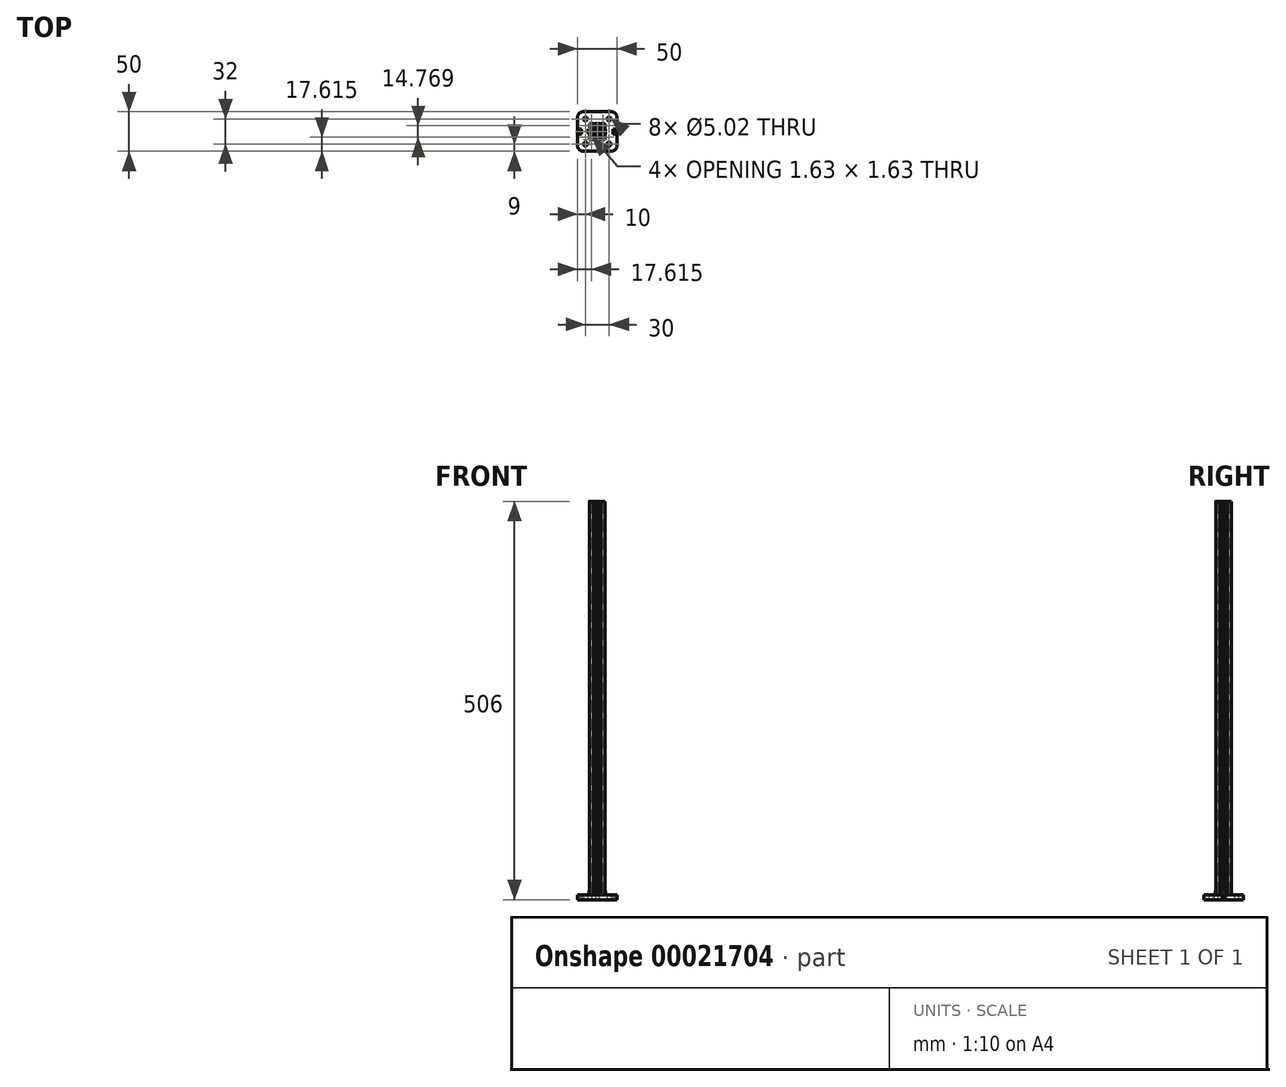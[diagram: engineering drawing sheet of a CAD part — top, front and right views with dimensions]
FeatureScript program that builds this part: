
annotation { "Feature Type Name" : "Feature", "Feature Type Description" : "" }
export const myFeature = defineFeature(function(context is Context, id is Id, definition is map)
    precondition{}
    {
        {
            var Q0;
            Q0=qCreatedBy(makeId("Top.planeOp"),FACE);
            var sketch = newSketch(context, id + "F4", { "sketchPlane" : qUnion([Q0])});
            skLineSegment(sketch, "E0", {"start": v(0, 0) * mm, "end": v(0, 25) * mm, "construction": true});
            skLineSegment(sketch, "E1", {"start": v(0, 0) * mm, "end": v(25, 0) * mm, "construction": true});
            skLineSegment(sketch, "E2", {"start": v(25, 0) * mm, "end": v(25, 18.3) * mm});
            skLineSegment(sketch, "E3", {"start": v(18.3, 25) * mm, "end": v(0, 25) * mm});
            skCircle(sketch, "E4", {"center": v(0, 0) * mm, "radius": 2.5 * mm, "construction": true});
            skLineSegment(sketch, "E5", {"start": v(15, 0) * mm, "end": v(15, 16) * mm, "construction": true});
            skLineSegment(sketch, "E6", {"start": v(15, 16) * mm, "end": v(0, 16) * mm, "construction": true});
            skCircle(sketch, "E7", {"center": v(15, 16) * mm, "radius": 2.5 * mm});
            skPoint(sketch, "E8.visualSharp", {"position": v(25, 25) * mm});
            skArc(sketch, "E8.filletArc", {"start": v(25, 18.3) * mm, "mid": v(23.04, 23.04) * mm, "end": v(18.3, 25) * mm});
            skLineSegment(sketch, "E9", {"start": v(22.26, 0) * mm, "end": v(22.26, 3.35) * mm});
            skLineSegment(sketch, "E10", {"start": v(22.26, 3.35) * mm, "end": v(25, 3.35) * mm});
            skLineSegment(sketch, "E11", {"start": v(22.26, 3.35) * mm, "end": v(20.26, 3.35) * mm});
            skLineSegment(sketch, "E12", {"start": v(20.26, 3.35) * mm, "end": v(20.26, 0) * mm});
            skCircle(sketch, "E13", {"center": v(10, 0) * mm, "radius": 2.5 * mm, "construction": true});
            skCircle(sketch, "E14", {"center": v(0, 10) * mm, "radius": 2.5 * mm, "construction": true});
            skLineSegment(sketch, "E15", {"start": v(10, 0) * mm, "end": v(0, 0) * mm, "construction": true});
            skLineSegment(sketch, "E16", {"start": v(0, 10) * mm, "end": v(0, 0) * mm, "construction": true});
            skArc(sketch, "E17", {"start": v(2.5, 0) * mm, "mid": v(1.77, 1.77) * mm, "end": v(0, 2.5) * mm});
            skArc(sketch, "E18", {"start": v(12.5, 0) * mm, "mid": v(10, 2.51) * mm, "end": v(7.5, 0) * mm});
            skArc(sketch, "E19", {"start": v(0, 7.5) * mm, "mid": v(2.5, 10) * mm, "end": v(0, 12.5) * mm});
            skArc(sketch, "E20.MirrorCS", {"start": v(0, 7.5) * mm, "mid": v(-2.5, 10) * mm, "end": v(0, 12.5) * mm});
            skArc(sketch, "E21.MirrorCS", {"start": v(-2.5, 0) * mm, "mid": v(-1.77, 1.77) * mm, "end": v(0, 2.5) * mm});
            skArc(sketch, "E22.MirrorCS", {"start": v(-12.5, 0) * mm, "mid": v(-10, 2.51) * mm, "end": v(-7.5, 0) * mm});
            skLineSegment(sketch, "E23.MirrorCS", {"start": v(-18.3, 25) * mm, "end": v(0, 25) * mm});
            skArc(sketch, "E24.MirrorCS", {"start": v(-25, 18.3) * mm, "mid": v(-23.04, 23.04) * mm, "end": v(-18.3, 25) * mm});
            skLineSegment(sketch, "E25.MirrorCS", {"start": v(-25, 0) * mm, "end": v(-25, 18.3) * mm});
            skLineSegment(sketch, "E26.MirrorCS", {"start": v(-22.26, 3.35) * mm, "end": v(-25, 3.35) * mm});
            skLineSegment(sketch, "E27.MirrorCS", {"start": v(-22.26, 0) * mm, "end": v(-22.26, 3.35) * mm});
            skLineSegment(sketch, "E28.MirrorCS", {"start": v(-22.26, 3.35) * mm, "end": v(-20.26, 3.35) * mm});
            skLineSegment(sketch, "E29.MirrorCS", {"start": v(-20.26, 3.35) * mm, "end": v(-20.26, 0) * mm});
            skCircle(sketch, "E30.MirrorC", {"center": v(-15, 16) * mm, "radius": 2.5 * mm});
            skLineSegment(sketch, "E31.MirrorCS", {"start": v(-25, 0) * mm, "end": v(-25, -18.3) * mm});
            skLineSegment(sketch, "E32.MirrorCS", {"start": v(-22.26, -3.35) * mm, "end": v(-25, -3.35) * mm});
            skLineSegment(sketch, "E33.MirrorCS", {"start": v(-22.26, 0) * mm, "end": v(-22.26, -3.35) * mm});
            skLineSegment(sketch, "E34.MirrorCS", {"start": v(-20.26, -3.35) * mm, "end": v(-20.26, 0) * mm});
            skLineSegment(sketch, "E35.MirrorCS", {"start": v(-22.26, -3.35) * mm, "end": v(-20.26, -3.35) * mm});
            skArc(sketch, "E36.MirrorCS", {"start": v(-12.5, 0) * mm, "mid": v(-10, -2.51) * mm, "end": v(-7.5, 0) * mm});
            skCircle(sketch, "E37.MirrorC", {"center": v(-15, -16) * mm, "radius": 2.5 * mm});
            skLineSegment(sketch, "E38.MirrorCS", {"start": v(-18.3, -25) * mm, "end": v(0, -25) * mm});
            skArc(sketch, "E39.MirrorCS", {"start": v(-25, -18.3) * mm, "mid": v(-23.04, -23.04) * mm, "end": v(-18.3, -25) * mm});
            skArc(sketch, "E40.MirrorCS", {"start": v(-2.5, 0) * mm, "mid": v(-1.77, -1.77) * mm, "end": v(0, -2.5) * mm});
            skArc(sketch, "E41.MirrorCS", {"start": v(2.5, 0) * mm, "mid": v(1.77, -1.77) * mm, "end": v(0, -2.5) * mm});
            skArc(sketch, "E42.MirrorCS", {"start": v(0, -7.5) * mm, "mid": v(2.5, -10) * mm, "end": v(0, -12.5) * mm});
            skArc(sketch, "E43.MirrorCS", {"start": v(0, -7.5) * mm, "mid": v(-2.5, -10) * mm, "end": v(0, -12.5) * mm});
            skArc(sketch, "E44.MirrorCS", {"start": v(12.5, 0) * mm, "mid": v(10, -2.51) * mm, "end": v(7.5, 0) * mm});
            skCircle(sketch, "E45.MirrorC", {"center": v(15, -16) * mm, "radius": 2.5 * mm});
            skLineSegment(sketch, "E46.MirrorCS", {"start": v(18.3, -25) * mm, "end": v(0, -25) * mm});
            skArc(sketch, "E47.MirrorCS", {"start": v(25, -18.3) * mm, "mid": v(23.04, -23.04) * mm, "end": v(18.3, -25) * mm});
            skLineSegment(sketch, "E48.MirrorCS", {"start": v(25, 0) * mm, "end": v(25, -18.3) * mm});
            skLineSegment(sketch, "E49.MirrorCS", {"start": v(20.26, -3.35) * mm, "end": v(20.26, 0) * mm});
            skLineSegment(sketch, "E50.MirrorCS", {"start": v(22.26, -3.35) * mm, "end": v(20.26, -3.35) * mm});
            skLineSegment(sketch, "E51.MirrorCS", {"start": v(22.26, 0) * mm, "end": v(22.26, -3.35) * mm});
            skLineSegment(sketch, "E52.MirrorCS", {"start": v(22.26, -3.35) * mm, "end": v(25, -3.35) * mm});
            skSolve(sketch);
        }
        {
            var Q0;
            Q0=makeQuery(id+"F4.imprint","IMPRINT",FACE,{"disambiguationData":[TD([[makeQuery(id+"F4.imprint","IMPRINT",EDGE,{"derivedFrom":sQuery(id+"F4.wireOp",EDGE,"E3")}),1.0]])]});
            var Q1;
            Q1=makeQuery(id+"F4.imprint","IMPRINT",FACE,{"disambiguationData":[TD([[makeQuery(id+"F4.imprint","IMPRINT",EDGE,{"derivedFrom":sQuery(id+"F4.wireOp",EDGE,"E22.MirrorCS")}),-1.0]])]});
            var Q2;
            Q2=makeQuery(id+"F4.imprint","IMPRINT",FACE,{"disambiguationData":[TD([[makeQuery(id+"F4.imprint","IMPRINT",EDGE,{"derivedFrom":sQuery(id+"F4.wireOp",EDGE,"E19")}),1.0]])]});
            var Q3;
            Q3=makeQuery(id+"F4.imprint","IMPRINT",FACE,{"disambiguationData":[TD([[makeQuery(id+"F4.imprint","IMPRINT",EDGE,{"derivedFrom":sQuery(id+"F4.wireOp",EDGE,"E18")}),1.0]])]});
            var Q4;
            Q4=makeQuery(id+"F4.imprint","IMPRINT",FACE,{"disambiguationData":[TD([[makeQuery(id+"F4.imprint","IMPRINT",EDGE,{"derivedFrom":sQuery(id+"F4.wireOp",EDGE,"E42.MirrorCS")}),-1.0]])]});
            extrude(context, id + "F0", {"entities" : qUnion([Q0, Q1, Q2, Q3, Q4]), "depth" : 6 * mm});
        }
        {
            var Q0;
            {var subQ4=sQuery(id+"F4.wireOp",EDGE,"E26.MirrorCS");Q0=makeQuery(id+"F4.imprint","IMPRINT",FACE,{"disambiguationData":[TD([[makeQuery(id+"F4.imprint","IMPRINT",EDGE,{"derivedFrom":subQ4}),1.0]])]});}
            var Q1;
            Q1=makeQuery(id+"F4.imprint","IMPRINT",FACE,{"disambiguationData":[TD([[makeQuery(id+"F4.imprint","IMPRINT",EDGE,{"derivedFrom":sQuery(id+"F4.wireOp",EDGE,"E9")}),-1.0]])]});
            extrude(context, id + "F5", {"entities" : qUnion([Q0, Q1]), "operationType" : NewBodyOperationType.ADD, "depth" : 4 * mm});
        }
        {
            var Q0;
            Q0=makeQuery(id+"F0.opExtrude","CAP_FACE",FACE,{"disambiguationData":[OSD([sQuery(id+"F4.wireOp",EDGE,"E2"),sQuery(id+"F4.wireOp",EDGE,"E3"),sQuery(id+"F4.wireOp",EDGE,"E7"),sQuery(id+"F4.wireOp",EDGE,"E8.filletArc"),sQuery(id+"F4.wireOp",EDGE,"E10"),sQuery(id+"F4.wireOp",EDGE,"E11"),sQuery(id+"F4.wireOp",EDGE,"E12"),sQuery(id+"F4.wireOp",EDGE,"E17"),sQuery(id+"F4.wireOp",EDGE,"E18"),sQuery(id+"F4.wireOp",EDGE,"E19"),sQuery(id+"F4.wireOp",EDGE,"E20.MirrorCS"),sQuery(id+"F4.wireOp",EDGE,"E21.MirrorCS"),sQuery(id+"F4.wireOp",EDGE,"E22.MirrorCS"),sQuery(id+"F4.wireOp",EDGE,"E23.MirrorCS"),sQuery(id+"F4.wireOp",EDGE,"E24.MirrorCS"),sQuery(id+"F4.wireOp",EDGE,"E25.MirrorCS"),sQuery(id+"F4.wireOp",EDGE,"E26.MirrorCS"),sQuery(id+"F4.wireOp",EDGE,"E28.MirrorCS"),sQuery(id+"F4.wireOp",EDGE,"E29.MirrorCS"),sQuery(id+"F4.wireOp",EDGE,"E30.MirrorC"),sQuery(id+"F4.wireOp",EDGE,"E31.MirrorCS"),sQuery(id+"F4.wireOp",EDGE,"E32.MirrorCS"),sQuery(id+"F4.wireOp",EDGE,"E34.MirrorCS"),sQuery(id+"F4.wireOp",EDGE,"E35.MirrorCS"),sQuery(id+"F4.wireOp",EDGE,"E36.MirrorCS"),sQuery(id+"F4.wireOp",EDGE,"E37.MirrorC"),sQuery(id+"F4.wireOp",EDGE,"E38.MirrorCS"),sQuery(id+"F4.wireOp",EDGE,"E39.MirrorCS"),sQuery(id+"F4.wireOp",EDGE,"E40.MirrorCS"),sQuery(id+"F4.wireOp",EDGE,"E41.MirrorCS"),sQuery(id+"F4.wireOp",EDGE,"E42.MirrorCS"),sQuery(id+"F4.wireOp",EDGE,"E43.MirrorCS"),sQuery(id+"F4.wireOp",EDGE,"E44.MirrorCS"),sQuery(id+"F4.wireOp",EDGE,"E45.MirrorC"),sQuery(id+"F4.wireOp",EDGE,"E46.MirrorCS"),sQuery(id+"F4.wireOp",EDGE,"E47.MirrorCS"),sQuery(id+"F4.wireOp",EDGE,"E48.MirrorCS"),sQuery(id+"F4.wireOp",EDGE,"E49.MirrorCS"),sQuery(id+"F4.wireOp",EDGE,"E50.MirrorCS"),sQuery(id+"F4.wireOp",EDGE,"E52.MirrorCS")])],"isStart":false});
            var sketch = newSketch(context, id + "F1", { "sketchPlane" : qUnion([Q0])});
            skLineSegment(sketch, "E53", {"start": v(2.73, 0) * mm, "end": v(-2.73, 0) * mm, "construction": true});
            skLineSegment(sketch, "E54", {"start": v(0, 2.73) * mm, "end": v(0, -2.73) * mm, "construction": true});
            skArc(sketch, "E55", {"start": v(-8.5, 10) * mm, "mid": v(-9.56, 9.56) * mm, "end": v(-10, 8.5) * mm});
            skLineSegment(sketch, "E56", {"start": v(-10, 8.5) * mm, "end": v(-10, 4.64) * mm});
            skLineSegment(sketch, "E57", {"start": v(-10, 4.64) * mm, "end": v(-8.2, 2.84) * mm});
            skLineSegment(sketch, "E58", {"start": v(-8.2, 5.5) * mm, "end": v(-8.2, 2.84) * mm});
            skLineSegment(sketch, "E59", {"start": v(-8.2, 5.5) * mm, "end": v(-6.56, 5.5) * mm});
            skLineSegment(sketch, "E60", {"start": v(-6.56, 5.5) * mm, "end": v(-3.9, 2.84) * mm});
            skLineSegment(sketch, "E61", {"start": v(-3.9, 2.84) * mm, "end": v(-3.9, 0.2) * mm});
            skLineSegment(sketch, "E62", {"start": v(-3.9, 0.2) * mm, "end": v(-3.7, 0) * mm});
            skLineSegment(sketch, "E63", {"start": v(-0.2, 3.9) * mm, "end": v(0, 3.7) * mm});
            skLineSegment(sketch, "E64", {"start": v(-0.2, 3.9) * mm, "end": v(-2.84, 3.9) * mm});
            skLineSegment(sketch, "E65", {"start": v(-5.5, 6.56) * mm, "end": v(-2.84, 3.9) * mm});
            skLineSegment(sketch, "E66", {"start": v(-5.5, 8.2) * mm, "end": v(-5.5, 6.56) * mm});
            skLineSegment(sketch, "E67", {"start": v(-2.84, 8.2) * mm, "end": v(-5.5, 8.2) * mm});
            skLineSegment(sketch, "E68", {"start": v(-4.64, 10) * mm, "end": v(-2.84, 8.2) * mm});
            skLineSegment(sketch, "E69", {"start": v(-8.5, 10) * mm, "end": v(-4.64, 10) * mm});
            skCircle(sketch, "E70", {"center": v(0, 0) * mm, "radius": 2.1 * mm});
            skLineSegment(sketch, "E71", {"start": v(-6.57, 8.2) * mm, "end": v(-8.2, 8.2) * mm});
            skLineSegment(sketch, "E72", {"start": v(-6.57, 8.2) * mm, "end": v(-6.57, 7.63) * mm});
            skLineSegment(sketch, "E73", {"start": v(-7.63, 6.57) * mm, "end": v(-6.57, 7.63) * mm});
            skLineSegment(sketch, "E74", {"start": v(-8.2, 6.57) * mm, "end": v(-7.63, 6.57) * mm});
            skLineSegment(sketch, "E75", {"start": v(-8.2, 8.2) * mm, "end": v(-8.2, 6.57) * mm});
            skLineSegment(sketch, "E76.MirrorCS", {"start": v(0.2, 3.9) * mm, "end": v(0, 3.7) * mm});
            skLineSegment(sketch, "E77.MirrorCS", {"start": v(0.2, 3.9) * mm, "end": v(2.84, 3.9) * mm});
            skLineSegment(sketch, "E78.MirrorCS", {"start": v(5.5, 6.56) * mm, "end": v(2.84, 3.9) * mm});
            skLineSegment(sketch, "E79.MirrorCS", {"start": v(5.5, 8.2) * mm, "end": v(5.5, 6.56) * mm});
            skLineSegment(sketch, "E80.MirrorCS", {"start": v(2.84, 8.2) * mm, "end": v(5.5, 8.2) * mm});
            skLineSegment(sketch, "E81.MirrorCS", {"start": v(4.64, 10) * mm, "end": v(2.84, 8.2) * mm});
            skLineSegment(sketch, "E82.MirrorCS", {"start": v(8.5, 10) * mm, "end": v(4.64, 10) * mm});
            skArc(sketch, "E83.MirrorCS", {"start": v(8.5, 10) * mm, "mid": v(9.56, 9.56) * mm, "end": v(10, 8.5) * mm});
            skLineSegment(sketch, "E84.MirrorCS", {"start": v(10, 8.5) * mm, "end": v(10, 4.64) * mm});
            skLineSegment(sketch, "E85.MirrorCS", {"start": v(8.2, 8.2) * mm, "end": v(8.2, 6.57) * mm});
            skLineSegment(sketch, "E86.MirrorCS", {"start": v(6.57, 8.2) * mm, "end": v(8.2, 8.2) * mm});
            skLineSegment(sketch, "E87.MirrorCS", {"start": v(6.57, 8.2) * mm, "end": v(6.57, 7.63) * mm});
            skLineSegment(sketch, "E88.MirrorCS", {"start": v(7.63, 6.57) * mm, "end": v(6.57, 7.63) * mm});
            skLineSegment(sketch, "E89.MirrorCS", {"start": v(8.2, 6.57) * mm, "end": v(7.63, 6.57) * mm});
            skLineSegment(sketch, "E90.MirrorCS", {"start": v(10, 4.64) * mm, "end": v(8.2, 2.84) * mm});
            skLineSegment(sketch, "E91.MirrorCS", {"start": v(8.2, 5.5) * mm, "end": v(8.2, 2.84) * mm});
            skLineSegment(sketch, "E92.MirrorCS", {"start": v(8.2, 5.5) * mm, "end": v(6.56, 5.5) * mm});
            skLineSegment(sketch, "E93.MirrorCS", {"start": v(6.56, 5.5) * mm, "end": v(3.9, 2.84) * mm});
            skLineSegment(sketch, "E94.MirrorCS", {"start": v(3.9, 2.84) * mm, "end": v(3.9, 0.2) * mm});
            skLineSegment(sketch, "E95.MirrorCS", {"start": v(3.9, 0.2) * mm, "end": v(3.7, 0) * mm});
            skLineSegment(sketch, "E96.MirrorCS", {"start": v(3.9, -0.2) * mm, "end": v(3.7, 0) * mm});
            skLineSegment(sketch, "E97.MirrorCS", {"start": v(6.57, -8.2) * mm, "end": v(6.57, -7.63) * mm});
            skLineSegment(sketch, "E98.MirrorCS", {"start": v(8.2, -6.57) * mm, "end": v(7.63, -6.57) * mm});
            skLineSegment(sketch, "E99.MirrorCS", {"start": v(7.63, -6.57) * mm, "end": v(6.57, -7.63) * mm});
            skLineSegment(sketch, "E100.MirrorCS", {"start": v(5.5, -8.2) * mm, "end": v(5.5, -6.56) * mm});
            skLineSegment(sketch, "E101.MirrorCS", {"start": v(4.64, -10) * mm, "end": v(2.84, -8.2) * mm});
            skLineSegment(sketch, "E102.MirrorCS", {"start": v(2.84, -8.2) * mm, "end": v(5.5, -8.2) * mm});
            skLineSegment(sketch, "E103.MirrorCS", {"start": v(10, -8.5) * mm, "end": v(10, -4.64) * mm});
            skLineSegment(sketch, "E104.MirrorCS", {"start": v(8.2, -5.5) * mm, "end": v(6.56, -5.5) * mm});
            skLineSegment(sketch, "E105.MirrorCS", {"start": v(5.5, -6.56) * mm, "end": v(2.84, -3.9) * mm});
            skLineSegment(sketch, "E106.MirrorCS", {"start": v(8.2, -8.2) * mm, "end": v(8.2, -6.57) * mm});
            skLineSegment(sketch, "E107.MirrorCS", {"start": v(8.2, -5.5) * mm, "end": v(8.2, -2.84) * mm});
            skLineSegment(sketch, "E108.MirrorCS", {"start": v(6.56, -5.5) * mm, "end": v(3.9, -2.84) * mm});
            skArc(sketch, "E109.MirrorCS", {"start": v(8.5, -10) * mm, "mid": v(9.56, -9.56) * mm, "end": v(10, -8.5) * mm});
            skLineSegment(sketch, "E110.MirrorCS", {"start": v(10, -4.64) * mm, "end": v(8.2, -2.84) * mm});
            skLineSegment(sketch, "E111.MirrorCS", {"start": v(6.57, -8.2) * mm, "end": v(8.2, -8.2) * mm});
            skLineSegment(sketch, "E112.MirrorCS", {"start": v(8.5, -10) * mm, "end": v(4.64, -10) * mm});
            skLineSegment(sketch, "E113.MirrorCS", {"start": v(3.9, -2.84) * mm, "end": v(3.9, -0.2) * mm});
            skLineSegment(sketch, "E114.MirrorCS", {"start": v(0.2, -3.9) * mm, "end": v(2.84, -3.9) * mm});
            skLineSegment(sketch, "E115.MirrorCS", {"start": v(0.2, -3.9) * mm, "end": v(0, -3.7) * mm});
            skLineSegment(sketch, "E116.MirrorCS", {"start": v(-0.2, -3.9) * mm, "end": v(0, -3.7) * mm});
            skLineSegment(sketch, "E117.MirrorCS", {"start": v(-0.2, -3.9) * mm, "end": v(-2.84, -3.9) * mm});
            skLineSegment(sketch, "E118.MirrorCS", {"start": v(-5.5, -6.56) * mm, "end": v(-2.84, -3.9) * mm});
            skLineSegment(sketch, "E119.MirrorCS", {"start": v(-5.5, -8.2) * mm, "end": v(-5.5, -6.56) * mm});
            skLineSegment(sketch, "E120.MirrorCS", {"start": v(-4.64, -10) * mm, "end": v(-2.84, -8.2) * mm});
            skLineSegment(sketch, "E121.MirrorCS", {"start": v(-2.84, -8.2) * mm, "end": v(-5.5, -8.2) * mm});
            skLineSegment(sketch, "E122.MirrorCS", {"start": v(-8.5, -10) * mm, "end": v(-4.64, -10) * mm});
            skArc(sketch, "E123.MirrorCS", {"start": v(-8.5, -10) * mm, "mid": v(-9.56, -9.56) * mm, "end": v(-10, -8.5) * mm});
            skLineSegment(sketch, "E124.MirrorCS", {"start": v(-10, -8.5) * mm, "end": v(-10, -4.64) * mm});
            skLineSegment(sketch, "E125.MirrorCS", {"start": v(-8.2, -5.5) * mm, "end": v(-8.2, -2.84) * mm});
            skLineSegment(sketch, "E126.MirrorCS", {"start": v(-10, -4.64) * mm, "end": v(-8.2, -2.84) * mm});
            skLineSegment(sketch, "E127.MirrorCS", {"start": v(-8.2, -8.2) * mm, "end": v(-8.2, -6.57) * mm});
            skLineSegment(sketch, "E128.MirrorCS", {"start": v(-6.57, -8.2) * mm, "end": v(-8.2, -8.2) * mm});
            skLineSegment(sketch, "E129.MirrorCS", {"start": v(-6.57, -8.2) * mm, "end": v(-6.57, -7.63) * mm});
            skLineSegment(sketch, "E130.MirrorCS", {"start": v(-7.63, -6.57) * mm, "end": v(-6.57, -7.63) * mm});
            skLineSegment(sketch, "E131.MirrorCS", {"start": v(-8.2, -6.57) * mm, "end": v(-7.63, -6.57) * mm});
            skLineSegment(sketch, "E132.MirrorCS", {"start": v(-8.2, -5.5) * mm, "end": v(-6.56, -5.5) * mm});
            skLineSegment(sketch, "E133.MirrorCS", {"start": v(-6.56, -5.5) * mm, "end": v(-3.9, -2.84) * mm});
            skLineSegment(sketch, "E134.MirrorCS", {"start": v(-3.9, -2.84) * mm, "end": v(-3.9, -0.2) * mm});
            skLineSegment(sketch, "E135.MirrorCS", {"start": v(-3.9, -0.2) * mm, "end": v(-3.7, 0) * mm});
            skLineSegment(sketch, "E136.0", {"start": v(-5.1, 6.52) * mm, "end": v(-2.88, 4.3) * mm});
            skLineSegment(sketch, "E137.0", {"start": v(-5.25, 7.45) * mm, "end": v(-5.25, 6.87) * mm});
            skLineSegment(sketch, "E138.0", {"start": v(-2.84, 7.95) * mm, "end": v(-4.75, 7.95) * mm});
            skLineSegment(sketch, "E139.0", {"start": v(0, 4.15) * mm, "end": v(-2.53, 4.15) * mm});
            skLineSegment(sketch, "E140", {"start": v(0, 2.73) * mm, "end": v(0, 14.28) * mm, "construction": true});
            skLineSegment(sketch, "E141.MirrorCS", {"start": v(2.84, 7.95) * mm, "end": v(4.75, 7.95) * mm});
            skLineSegment(sketch, "E142.MirrorCS", {"start": v(5.25, 7.45) * mm, "end": v(5.25, 6.87) * mm});
            skLineSegment(sketch, "E143.MirrorCS", {"start": v(5.1, 6.52) * mm, "end": v(2.88, 4.3) * mm});
            skLineSegment(sketch, "E144.MirrorCS", {"start": v(0, 4.15) * mm, "end": v(2.53, 4.15) * mm});
            skLineSegment(sketch, "E145", {"start": v(0, 0) * mm, "end": v(8.5, 8.5) * mm, "construction": true});
            skLineSegment(sketch, "E146", {"start": v(8.5, -8.5) * mm, "end": v(-8.5, 8.5) * mm, "construction": true});
            skLineSegment(sketch, "E147.0", {"start": v(-3.6, 9.32) * mm, "end": v(-2.66, 8.38) * mm});
            skPoint(sketch, "E148.newPointB", {"position": v(0, 7.95) * mm});
            skArc(sketch, "E148.filletArc", {"start": v(-2.84, 7.95) * mm, "mid": v(-2.6, 8.1) * mm, "end": v(-2.66, 8.38) * mm});
            skLineSegment(sketch, "E149", {"start": v(-3.26, 10.18) * mm, "end": v(0, 10.18) * mm});
            skArc(sketch, "E150.MirrorCS", {"start": v(2.84, 7.95) * mm, "mid": v(2.6, 8.1) * mm, "end": v(2.66, 8.38) * mm});
            skLineSegment(sketch, "E151.MirrorCS", {"start": v(3.26, 10.18) * mm, "end": v(0, 10.18) * mm});
            skLineSegment(sketch, "E152.MirrorCS", {"start": v(3.6, 9.32) * mm, "end": v(2.66, 8.38) * mm});
            skPoint(sketch, "E153.visualSharp", {"position": v(-4.46, 10.18) * mm});
            skArc(sketch, "E153.filletArc", {"start": v(-3.26, 10.18) * mm, "mid": v(-3.72, 9.87) * mm, "end": v(-3.6, 9.32) * mm});
            skPoint(sketch, "E154.visualSharp", {"position": v(4.46, 10.18) * mm});
            skArc(sketch, "E154.filletArc", {"start": v(3.6, 9.32) * mm, "mid": v(3.72, 9.87) * mm, "end": v(3.26, 10.18) * mm});
            skPoint(sketch, "E155.visualSharp", {"position": v(5.25, 7.95) * mm});
            skArc(sketch, "E155.filletArc", {"start": v(5.25, 7.45) * mm, "mid": v(5.1, 7.8) * mm, "end": v(4.75, 7.95) * mm});
            skPoint(sketch, "E156.visualSharp", {"position": v(5.25, 6.66) * mm});
            skArc(sketch, "E156.filletArc", {"start": v(5.1, 6.52) * mm, "mid": v(5.21, 6.68) * mm, "end": v(5.25, 6.87) * mm});
            skPoint(sketch, "E157.visualSharp", {"position": v(2.74, 4.15) * mm});
            skArc(sketch, "E157.filletArc", {"start": v(2.53, 4.15) * mm, "mid": v(2.72, 4.19) * mm, "end": v(2.88, 4.3) * mm});
            skPoint(sketch, "E158.visualSharp", {"position": v(-2.74, 4.15) * mm});
            skArc(sketch, "E158.filletArc", {"start": v(-2.88, 4.3) * mm, "mid": v(-2.72, 4.19) * mm, "end": v(-2.53, 4.15) * mm});
            skPoint(sketch, "E159.visualSharp", {"position": v(-5.25, 6.66) * mm});
            skArc(sketch, "E159.filletArc", {"start": v(-5.25, 6.87) * mm, "mid": v(-5.21, 6.68) * mm, "end": v(-5.1, 6.52) * mm});
            skPoint(sketch, "E160.visualSharp", {"position": v(-5.25, 7.95) * mm});
            skArc(sketch, "E160.filletArc", {"start": v(-4.75, 7.95) * mm, "mid": v(-5.1, 7.8) * mm, "end": v(-5.25, 7.45) * mm});
            skLineSegment(sketch, "E161.1.0", {"start": v(-10.18, -3.26) * mm, "end": v(-10.18, 0) * mm});
            skArc(sketch, "E161.1.1", {"start": v(-10.18, -3.26) * mm, "mid": v(-9.87, -3.72) * mm, "end": v(-9.32, -3.6) * mm});
            skLineSegment(sketch, "E161.1.2", {"start": v(-9.32, -3.6) * mm, "end": v(-8.38, -2.66) * mm});
            skArc(sketch, "E161.1.3", {"start": v(-7.95, -2.84) * mm, "mid": v(-8.1, -2.6) * mm, "end": v(-8.38, -2.66) * mm});
            skLineSegment(sketch, "E161.1.4", {"start": v(-7.95, -2.84) * mm, "end": v(-7.95, -4.75) * mm});
            skArc(sketch, "E161.1.5", {"start": v(-7.95, -4.75) * mm, "mid": v(-7.8, -5.1) * mm, "end": v(-7.45, -5.25) * mm});
            skLineSegment(sketch, "E161.1.6", {"start": v(-7.45, -5.25) * mm, "end": v(-6.87, -5.25) * mm});
            skArc(sketch, "E161.1.7", {"start": v(-6.87, -5.25) * mm, "mid": v(-6.68, -5.21) * mm, "end": v(-6.52, -5.1) * mm});
            skLineSegment(sketch, "E161.1.8", {"start": v(-6.52, -5.1) * mm, "end": v(-4.3, -2.88) * mm});
            skArc(sketch, "E161.1.9", {"start": v(-4.3, -2.88) * mm, "mid": v(-4.19, -2.72) * mm, "end": v(-4.15, -2.53) * mm});
            skLineSegment(sketch, "E161.1.10", {"start": v(-4.15, 0) * mm, "end": v(-4.15, -2.53) * mm});
            skLineSegment(sketch, "E161.1.11", {"start": v(-4.15, 0) * mm, "end": v(-4.15, 2.53) * mm});
            skArc(sketch, "E161.1.12", {"start": v(-4.15, 2.53) * mm, "mid": v(-4.19, 2.72) * mm, "end": v(-4.3, 2.88) * mm});
            skLineSegment(sketch, "E161.1.13", {"start": v(-6.52, 5.1) * mm, "end": v(-4.3, 2.88) * mm});
            skArc(sketch, "E161.1.14", {"start": v(-6.52, 5.1) * mm, "mid": v(-6.68, 5.21) * mm, "end": v(-6.87, 5.25) * mm});
            skLineSegment(sketch, "E161.1.15", {"start": v(-7.45, 5.25) * mm, "end": v(-6.87, 5.25) * mm});
            skArc(sketch, "E161.1.16", {"start": v(-7.45, 5.25) * mm, "mid": v(-7.8, 5.1) * mm, "end": v(-7.95, 4.75) * mm});
            skLineSegment(sketch, "E161.1.17", {"start": v(-7.95, 2.84) * mm, "end": v(-7.95, 4.75) * mm});
            skArc(sketch, "E161.1.18", {"start": v(-7.95, 2.84) * mm, "mid": v(-8.1, 2.6) * mm, "end": v(-8.38, 2.66) * mm});
            skLineSegment(sketch, "E161.1.19", {"start": v(-9.32, 3.6) * mm, "end": v(-8.38, 2.66) * mm});
            skArc(sketch, "E161.1.20", {"start": v(-9.32, 3.6) * mm, "mid": v(-9.87, 3.72) * mm, "end": v(-10.18, 3.26) * mm});
            skLineSegment(sketch, "E161.1.21", {"start": v(-10.18, 3.26) * mm, "end": v(-10.18, 0) * mm});
            skLineSegment(sketch, "E161.2.0", {"start": v(3.26, -10.18) * mm, "end": v(0, -10.18) * mm});
            skArc(sketch, "E161.2.1", {"start": v(3.26, -10.18) * mm, "mid": v(3.72, -9.87) * mm, "end": v(3.6, -9.32) * mm});
            skLineSegment(sketch, "E161.2.2", {"start": v(3.6, -9.32) * mm, "end": v(2.66, -8.38) * mm});
            skArc(sketch, "E161.2.3", {"start": v(2.84, -7.95) * mm, "mid": v(2.6, -8.1) * mm, "end": v(2.66, -8.38) * mm});
            skLineSegment(sketch, "E161.2.4", {"start": v(2.84, -7.95) * mm, "end": v(4.75, -7.95) * mm});
            skArc(sketch, "E161.2.5", {"start": v(4.75, -7.95) * mm, "mid": v(5.1, -7.8) * mm, "end": v(5.25, -7.45) * mm});
            skLineSegment(sketch, "E161.2.6", {"start": v(5.25, -7.45) * mm, "end": v(5.25, -6.87) * mm});
            skArc(sketch, "E161.2.7", {"start": v(5.25, -6.87) * mm, "mid": v(5.21, -6.68) * mm, "end": v(5.1, -6.52) * mm});
            skLineSegment(sketch, "E161.2.8", {"start": v(5.1, -6.52) * mm, "end": v(2.88, -4.3) * mm});
            skArc(sketch, "E161.2.9", {"start": v(2.88, -4.3) * mm, "mid": v(2.72, -4.19) * mm, "end": v(2.53, -4.15) * mm});
            skLineSegment(sketch, "E161.2.10", {"start": v(0, -4.15) * mm, "end": v(2.53, -4.15) * mm});
            skLineSegment(sketch, "E161.2.11", {"start": v(0, -4.15) * mm, "end": v(-2.53, -4.15) * mm});
            skArc(sketch, "E161.2.12", {"start": v(-2.53, -4.15) * mm, "mid": v(-2.72, -4.19) * mm, "end": v(-2.88, -4.3) * mm});
            skLineSegment(sketch, "E161.2.13", {"start": v(-5.1, -6.52) * mm, "end": v(-2.88, -4.3) * mm});
            skArc(sketch, "E161.2.14", {"start": v(-5.1, -6.52) * mm, "mid": v(-5.21, -6.68) * mm, "end": v(-5.25, -6.87) * mm});
            skLineSegment(sketch, "E161.2.15", {"start": v(-5.25, -7.45) * mm, "end": v(-5.25, -6.87) * mm});
            skArc(sketch, "E161.2.16", {"start": v(-5.25, -7.45) * mm, "mid": v(-5.1, -7.8) * mm, "end": v(-4.75, -7.95) * mm});
            skLineSegment(sketch, "E161.2.17", {"start": v(-2.84, -7.95) * mm, "end": v(-4.75, -7.95) * mm});
            skArc(sketch, "E161.2.18", {"start": v(-2.84, -7.95) * mm, "mid": v(-2.6, -8.1) * mm, "end": v(-2.66, -8.38) * mm});
            skLineSegment(sketch, "E161.2.19", {"start": v(-3.6, -9.32) * mm, "end": v(-2.66, -8.38) * mm});
            skArc(sketch, "E161.2.20", {"start": v(-3.6, -9.32) * mm, "mid": v(-3.72, -9.87) * mm, "end": v(-3.26, -10.18) * mm});
            skLineSegment(sketch, "E161.2.21", {"start": v(-3.26, -10.18) * mm, "end": v(0, -10.18) * mm});
            skLineSegment(sketch, "E161.3.0", {"start": v(10.18, 3.26) * mm, "end": v(10.18, 0) * mm});
            skArc(sketch, "E161.3.1", {"start": v(10.18, 3.26) * mm, "mid": v(9.87, 3.72) * mm, "end": v(9.32, 3.6) * mm});
            skLineSegment(sketch, "E161.3.2", {"start": v(9.32, 3.6) * mm, "end": v(8.38, 2.66) * mm});
            skArc(sketch, "E161.3.3", {"start": v(7.95, 2.84) * mm, "mid": v(8.1, 2.6) * mm, "end": v(8.38, 2.66) * mm});
            skLineSegment(sketch, "E161.3.4", {"start": v(7.95, 2.84) * mm, "end": v(7.95, 4.75) * mm});
            skArc(sketch, "E161.3.5", {"start": v(7.95, 4.75) * mm, "mid": v(7.8, 5.1) * mm, "end": v(7.45, 5.25) * mm});
            skLineSegment(sketch, "E161.3.6", {"start": v(7.45, 5.25) * mm, "end": v(6.87, 5.25) * mm});
            skArc(sketch, "E161.3.7", {"start": v(6.87, 5.25) * mm, "mid": v(6.68, 5.21) * mm, "end": v(6.52, 5.1) * mm});
            skLineSegment(sketch, "E161.3.8", {"start": v(6.52, 5.1) * mm, "end": v(4.3, 2.88) * mm});
            skArc(sketch, "E161.3.9", {"start": v(4.3, 2.88) * mm, "mid": v(4.19, 2.72) * mm, "end": v(4.15, 2.53) * mm});
            skLineSegment(sketch, "E161.3.10", {"start": v(4.15, 0) * mm, "end": v(4.15, 2.53) * mm});
            skLineSegment(sketch, "E161.3.11", {"start": v(4.15, 0) * mm, "end": v(4.15, -2.53) * mm});
            skArc(sketch, "E161.3.12", {"start": v(4.15, -2.53) * mm, "mid": v(4.19, -2.72) * mm, "end": v(4.3, -2.88) * mm});
            skLineSegment(sketch, "E161.3.13", {"start": v(6.52, -5.1) * mm, "end": v(4.3, -2.88) * mm});
            skArc(sketch, "E161.3.14", {"start": v(6.52, -5.1) * mm, "mid": v(6.68, -5.21) * mm, "end": v(6.87, -5.25) * mm});
            skLineSegment(sketch, "E161.3.15", {"start": v(7.45, -5.25) * mm, "end": v(6.87, -5.25) * mm});
            skArc(sketch, "E161.3.16", {"start": v(7.45, -5.25) * mm, "mid": v(7.8, -5.1) * mm, "end": v(7.95, -4.75) * mm});
            skLineSegment(sketch, "E161.3.17", {"start": v(7.95, -2.84) * mm, "end": v(7.95, -4.75) * mm});
            skArc(sketch, "E161.3.18", {"start": v(7.95, -2.84) * mm, "mid": v(8.1, -2.6) * mm, "end": v(8.38, -2.66) * mm});
            skLineSegment(sketch, "E161.3.19", {"start": v(9.32, -3.6) * mm, "end": v(8.38, -2.66) * mm});
            skArc(sketch, "E161.3.20", {"start": v(9.32, -3.6) * mm, "mid": v(9.87, -3.72) * mm, "end": v(10.18, -3.26) * mm});
            skLineSegment(sketch, "E161.3.21", {"start": v(10.18, -3.26) * mm, "end": v(10.18, 0) * mm});
            skSolve(sketch);
        }
        {
            var Q0;
            Q0=makeQuery(id+"F1.imprint","IMPRINT",FACE,{"disambiguationData":[TD([[makeQuery(id+"F1.imprint","IMPRINT",EDGE,{"derivedFrom":sQuery(id+"F1.wireOp",EDGE,"E136.0")}),1.0]])]});
            var Q1;
            Q1=makeQuery(id+"F1.imprint","IMPRINT",FACE,{"disambiguationData":[TD([[makeQuery(id+"F1.imprint","IMPRINT",EDGE,{"derivedFrom":sQuery(id+"F1.wireOp",EDGE,"97a04347-ffc2-4272-8581-b63b87e191c30.MirrorCS")}),1.0]])]});
            var Q2;
            {var subQ6=sQuery(id+"F1.wireOp",EDGE,"b754c6b4-6ef1-42a1-b540-394828c441de0.MirrorCS");Q2=makeQuery(id+"F1.imprint","IMPRINT",FACE,{"disambiguationData":[TD([[makeQuery(id+"F1.imprint","IMPRINT",EDGE,{"derivedFrom":subQ6}),-1.0]])]});}
            var Q3;
            Q3=makeQuery(id+"F1.imprint","IMPRINT",FACE,{"disambiguationData":[TD([[makeQuery(id+"F1.imprint","IMPRINT",EDGE,{"derivedFrom":sQuery(id+"F1.wireOp",EDGE,"dc0c365e-7566-4fdd-9898-c21d8e3a59930.MirrorCS")}),1.0]])]});
            var Q4;
            {var subQ1=sQuery(id+"F1.wireOp",EDGE,"E141.MirrorCS");var subQ3=sQuery(id+"F1.wireOp",EDGE,"E138.0");var subQ5=makeQuery(id+"F1.imprint","INTERSECT",VERTEX,{"derivedFrom":[subQ3,subQ1]});Q4=makeQuery(id+"F1.imprint","IMPRINT",FACE,{"disambiguationData":[TD([[makeQuery(id+"F1.imprint","IMPRINT",EDGE,{"disambiguationData":[TD([[subQ5,-1.0]])],"derivedFrom":subQ3}),1.0]])]});}
            var Q5;
            {var subQ1=sQuery(id+"F1.wireOp",EDGE,"4a798bb9-35ed-405a-be8e-6beaa67aea9b0.MirrorCS");var subQ3=sQuery(id+"F1.wireOp",EDGE,"765a75a6-8426-4268-bcc0-7f65aa6ce5040.MirrorCS");var subQ5=makeQuery(id+"F1.imprint","INTERSECT",VERTEX,{"derivedFrom":[subQ3,subQ1]});Q5=makeQuery(id+"F1.imprint","IMPRINT",FACE,{"disambiguationData":[TD([[makeQuery(id+"F1.imprint","IMPRINT",EDGE,{"disambiguationData":[TD([[subQ5,-1.0]])],"derivedFrom":subQ3}),1.0]])]});}
            var Q6;
            {var subQ1=sQuery(id+"F1.wireOp",EDGE,"61109fae-0632-4fd6-96c0-1158d4c46b1f0.MirrorCS");var subQ3=sQuery(id+"F1.wireOp",EDGE,"6bdf6139-cb56-45af-9e7b-c82a8b494dab0.MirrorCS");var subQ5=makeQuery(id+"F1.imprint","INTERSECT",VERTEX,{"derivedFrom":[subQ3,subQ1]});Q6=makeQuery(id+"F1.imprint","IMPRINT",FACE,{"disambiguationData":[TD([[makeQuery(id+"F1.imprint","IMPRINT",EDGE,{"disambiguationData":[TD([[subQ5,-1.0]])],"derivedFrom":subQ3}),-1.0]])]});}
            var Q7;
            {var subQ1=sQuery(id+"F1.wireOp",EDGE,"5f06026f-91d5-4f2f-9c34-d27ebdce79bf0.MirrorCS");var subQ3=sQuery(id+"F1.wireOp",EDGE,"f246371d-f16e-4b79-9ad7-26af30ad1bcb0.MirrorCS");var subQ5=makeQuery(id+"F1.imprint","INTERSECT",VERTEX,{"derivedFrom":[subQ3,subQ1]});Q7=makeQuery(id+"F1.imprint","IMPRINT",FACE,{"disambiguationData":[TD([[makeQuery(id+"F1.imprint","IMPRINT",EDGE,{"disambiguationData":[TD([[subQ5,-1.0]])],"derivedFrom":subQ3}),-1.0]])]});}
            var Q8;
            Q8=makeQuery(id+"F1.imprint","IMPRINT",FACE,{"disambiguationData":[TD([[makeQuery(id+"F1.imprint","IMPRINT",EDGE,{"derivedFrom":sQuery(id+"F1.wireOp",EDGE,"E161.1.0")}),-1.0]])]});
            var Q9;
            Q9=makeQuery(id+"F1.imprint","IMPRINT",FACE,{"disambiguationData":[TD([[makeQuery(id+"F1.imprint","IMPRINT",EDGE,{"derivedFrom":sQuery(id+"F1.wireOp",EDGE,"E161.3.0")}),-1.0]])]});
            var Q10;
            Q10=makeQuery(id+"F1.imprint","IMPRINT",FACE,{"disambiguationData":[TD([[makeQuery(id+"F1.imprint","IMPRINT",EDGE,{"derivedFrom":sQuery(id+"F1.wireOp",EDGE,"E161.2.0")}),-1.0]])]});
            extrude(context, id + "F2", {"entities" : qUnion([Q0, Q1, Q2, Q3, Q4, Q5, Q6, Q7, Q8, Q9, Q10]), "operationType" : NewBodyOperationType.ADD, "depth" : 5 * mm});
        }
        {
            var Q0;
            Q0=makeQuery(id+"F1.imprint","IMPRINT",FACE,{"disambiguationData":[TD([[makeQuery(id+"F1.imprint","IMPRINT",EDGE,{"derivedFrom":sQuery(id+"F1.wireOp",EDGE,"E55")}),1.0]])]});
            extrude(context, id + "F3", {"entities" : qUnion([Q0]), "depth" : 500 * mm});
        }
    });
